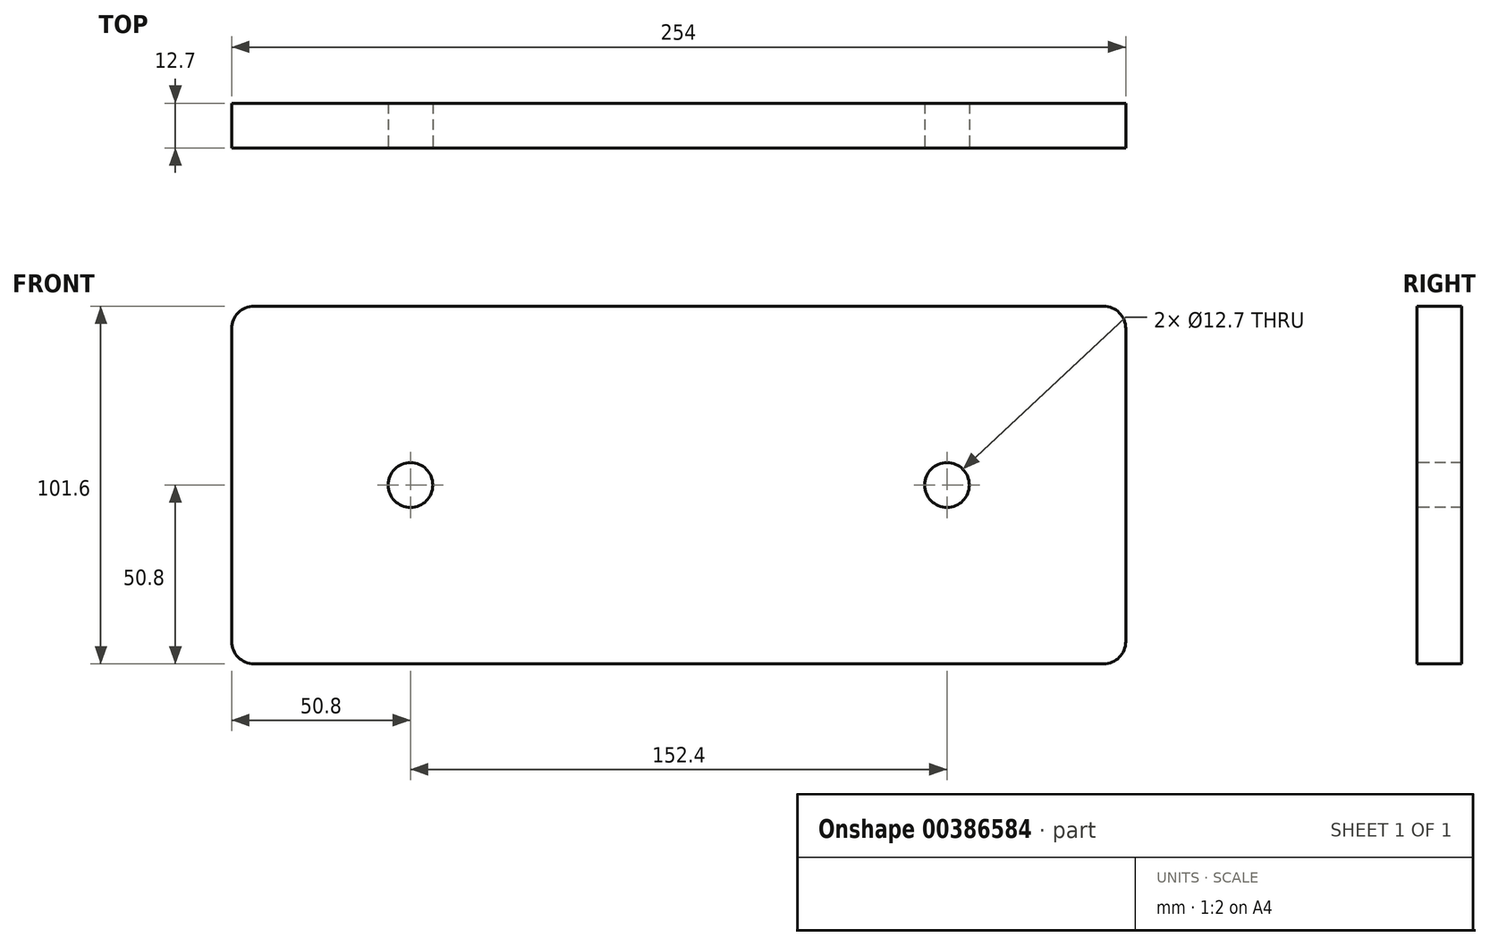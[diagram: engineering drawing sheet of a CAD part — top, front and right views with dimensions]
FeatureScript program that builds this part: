
annotation { "Feature Type Name" : "Feature", "Feature Type Description" : "" }
export const myFeature = defineFeature(function(context is Context, id is Id, definition is map)
    precondition{}
    {
        {
            var Q0;
            Q0=qCreatedBy(makeId("Front.planeOp"),FACE);
            var sketch = newSketch(context, id + "F0", { "sketchPlane" : qUnion([Q0])});
            skLineSegment(sketch, "E0.bottom", {"start": v(0, 0) * mm, "end": v(254, 0) * mm});
            skLineSegment(sketch, "E0.top", {"start": v(0, 101.6) * mm, "end": v(254, 101.6) * mm});
            skLineSegment(sketch, "E0.left", {"start": v(0, 0) * mm, "end": v(0, 101.6) * mm});
            skLineSegment(sketch, "E0.right", {"start": v(254, 0) * mm, "end": v(254, 101.6) * mm});
            skSolve(sketch);
        }
        {
            var Q0;
            Q0 = qSketchRegion(id + "F0", true);
            extrude(context, id + "F1", {"entities" : qUnion([Q0]), "depth" : 12.7 * mm});
        }
        {
            var Q0;
            Q0=makeQuery(id+"F1.opExtrude","SWEPT_EDGE",EDGE,{"disambiguationData":[OSD([sQuery(id+"F0.wireOp",EDGE,"E0.top"),sQuery(id+"F0.wireOp",EDGE,"E0.left")])]});
            var Q1;
            Q1=makeQuery(id+"F1.opExtrude","SWEPT_EDGE",EDGE,{"disambiguationData":[OSD([sQuery(id+"F0.wireOp",EDGE,"E0.bottom"),sQuery(id+"F0.wireOp",EDGE,"E0.left")])]});
            var Q2;
            Q2=makeQuery(id+"F1.opExtrude","SWEPT_EDGE",EDGE,{"disambiguationData":[OSD([sQuery(id+"F0.wireOp",EDGE,"E0.top"),sQuery(id+"F0.wireOp",EDGE,"E0.right")])]});
            var Q3;
            Q3=makeQuery(id+"F1.opExtrude","SWEPT_EDGE",EDGE,{"disambiguationData":[OSD([sQuery(id+"F0.wireOp",EDGE,"E0.bottom"),sQuery(id+"F0.wireOp",EDGE,"E0.right")])]});
            fillet(context, id + "F2", {"entities" : qUnion([Q0, Q1, Q2, Q3]), "radius" : 6.35 * mm, "tangentPropagation" : true, "allowEdgeOverflow" : false});
        }
        {
            var Q0;
            Q0=makeQuery(id+"F1.opExtrude","CAP_FACE",FACE,{"disambiguationData":[OSD([sQuery(id+"F0.wireOp",EDGE,"E0.bottom"),sQuery(id+"F0.wireOp",EDGE,"E0.top"),sQuery(id+"F0.wireOp",EDGE,"E0.left"),sQuery(id+"F0.wireOp",EDGE,"E0.right")])],"isStart":false});
            var sketch = newSketch(context, id + "F3", { "sketchPlane" : qUnion([Q0])});
            skPoint(sketch, "E1", {"position": v(50.8, 50.8) * mm});
            skPoint(sketch, "E2", {"position": v(203.2, 50.8) * mm});
            skSolve(sketch);
        }
        {
            var Q0;
            Q0=sQuery(id+"F3.wireOp",VERTEX,"E1");
            var Q1;
            Q1=sQuery(id+"F3.wireOp",VERTEX,"E2");
            var Q2;
            Q2=makeQuery(id+"F1.opExtrude","SWEPT_BODY",BODY,{"disambiguationData":[OSD([sQuery(id+"F0.wireOp",EDGE,"E0.bottom"),sQuery(id+"F0.wireOp",EDGE,"E0.top"),sQuery(id+"F0.wireOp",EDGE,"E0.left"),sQuery(id+"F0.wireOp",EDGE,"E0.right")])]});
            hole(context, id + "F4", {"style" : HoleStyle.SIMPLE, "endStyle" : HoleEndStyle.BLIND, "holeDiameter" : 12.7 * mm, "holeDepth" : 12.7 * mm, "isTappedThrough" : true, "tappedDepth" : 12.7 * mm, "tapClearance" : 3, "locations" : qUnion([Q0, Q1]), "scope" : qUnion([Q2])});
        }
    });
